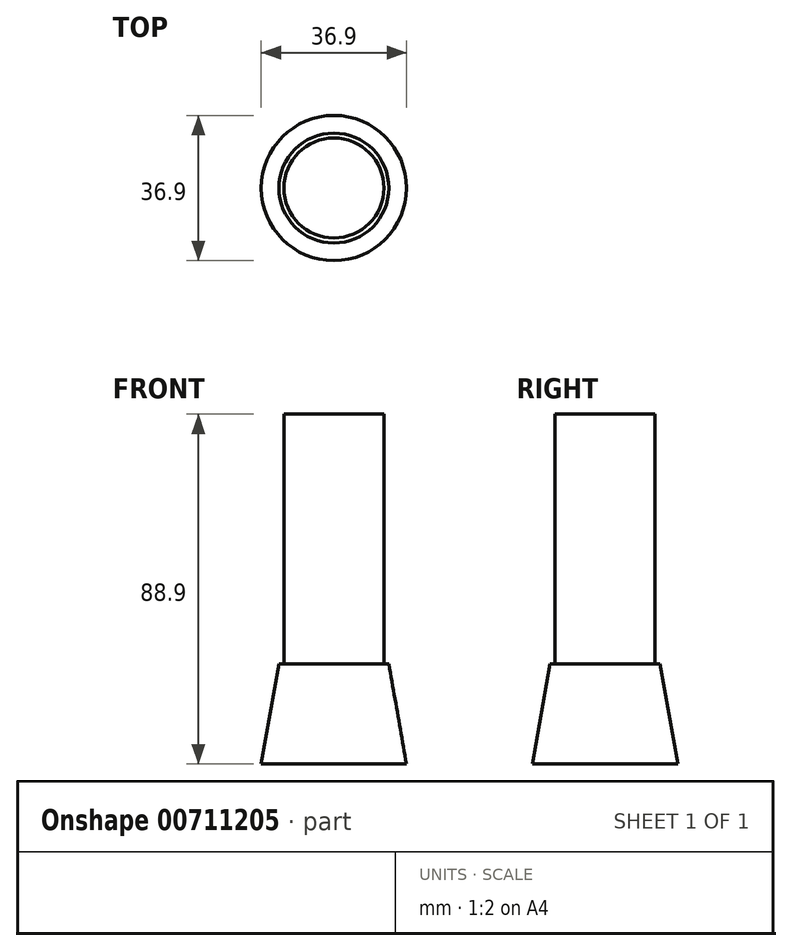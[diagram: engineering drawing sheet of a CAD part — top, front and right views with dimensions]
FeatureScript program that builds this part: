
annotation { "Feature Type Name" : "Feature", "Feature Type Description" : "" }
export const myFeature = defineFeature(function(context is Context, id is Id, definition is map)
    precondition{}
    {
        {
            var Q0;
            Q0=qCreatedBy(makeId("Top.planeOp"),FACE);
            var sketch = newSketch(context, id + "F0", { "sketchPlane" : qUnion([Q0])});
            skCircle(sketch, "E0", {"center": v(0, 0) * mm, "radius": 19.05 * mm});
            skCircle(sketch, "E1", {"center": v(0, 0) * mm, "radius": 12.7 * mm});
            skSolve(sketch);
        }
        {
            var Q0;
            Q0=makeQuery(id+"F0.imprint","IMPRINT",FACE,{"disambiguationData":[TD([[makeQuery(id+"F0.imprint","IMPRINT",EDGE,{"derivedFrom":sQuery(id+"F0.wireOp",EDGE,"E1")}),1.0]])]});
            extrude(context, id + "F1", {"entities" : qUnion([Q0]), "depth" : 88.9 * mm, "offsetDistance" : 25.4 * mm});
        }
        {
            var Q0;
            Q0 = qSketchRegion(id + "F0", true);
            extrude(context, id + "F2", {"entities" : qUnion([Q0]), "operationType" : NewBodyOperationType.ADD, "depth" : 25.4 * mm, "offsetDistance" : 25.4 * mm});
        }
        {
            var Q0;
            Q0=makeQuery(id+"F2.opExtrude","CAP_EDGE",EDGE,{"disambiguationData":[OSD([sQuery(id+"F0.wireOp",EDGE,"E0")])],"isStart":false});
            chamfer(context, id + "F3", {"entities" : qUnion([Q0]), "chamferType" : ChamferType.OFFSET_ANGLE, "width" : 5.08 * mm, "oppositeDirection" : false, "angle" : 80 * degree, "tangentPropagation" : true});
        }
    });
